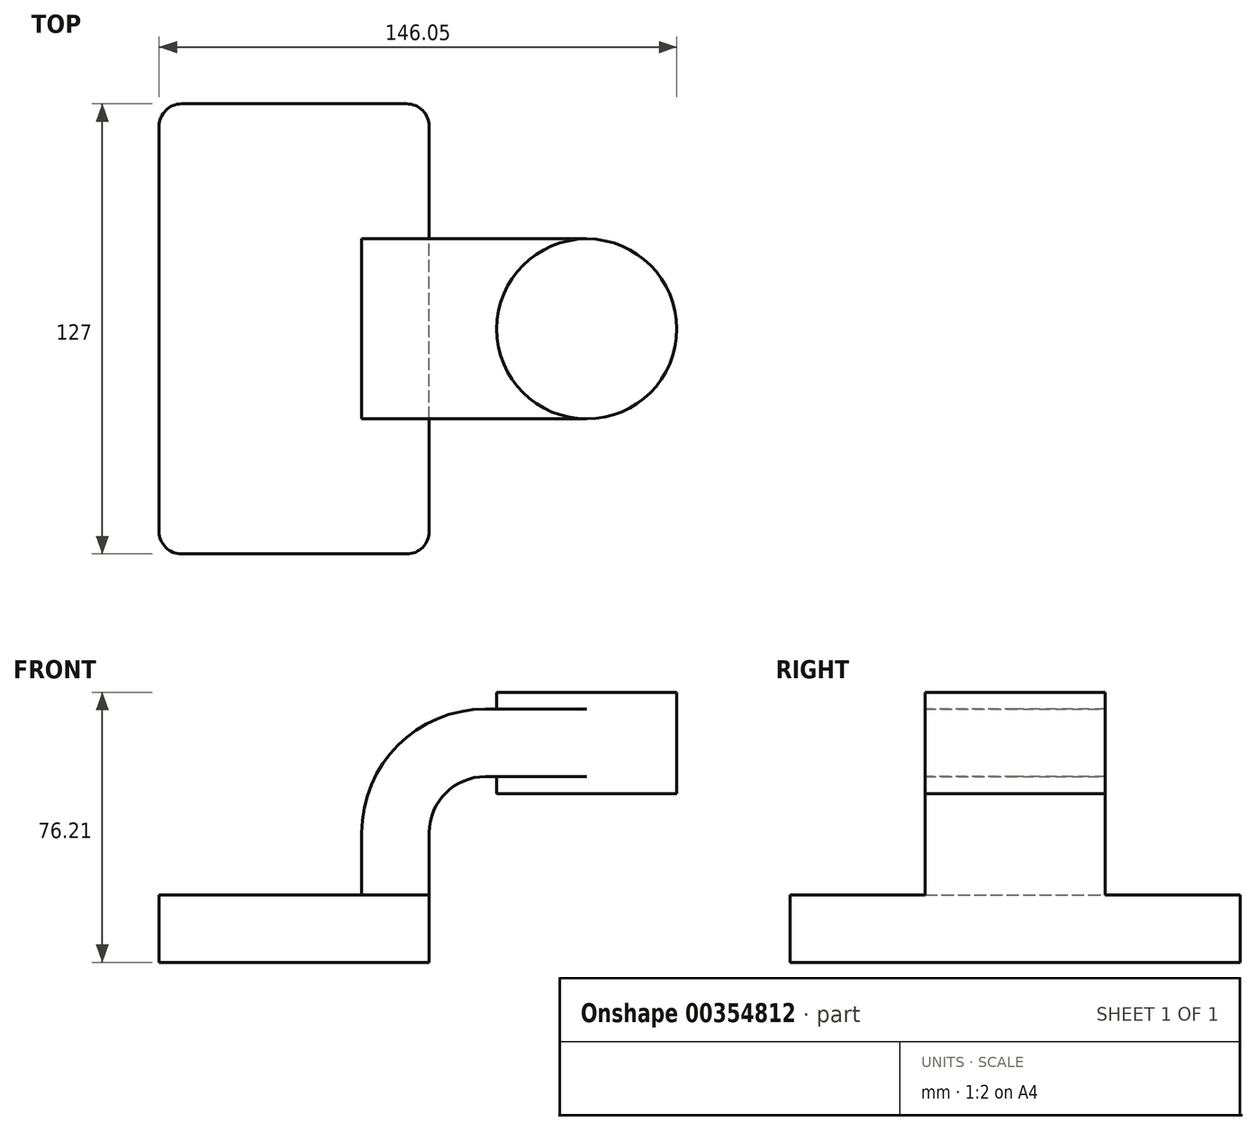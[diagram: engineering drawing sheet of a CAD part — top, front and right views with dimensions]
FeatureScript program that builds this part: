
annotation { "Feature Type Name" : "Feature", "Feature Type Description" : "" }
export const myFeature = defineFeature(function(context is Context, id is Id, definition is map)
    precondition{}
    {
        {
            var Q0;
            Q0=qCreatedBy(makeId("Front.planeOp"),FACE);
            var sketch = newSketch(context, id + "F0", { "sketchPlane" : qUnion([Q0])});
            skPoint(sketch, "E0.middle", {"position": v(0, 0) * mm});
            skLineSegment(sketch, "E1.bottom", {"start": v(-38.1, -9.53) * mm, "end": v(38.1, -9.53) * mm});
            skLineSegment(sketch, "E1.top", {"start": v(-38.1, 9.53) * mm, "end": v(38.1, 9.53) * mm});
            skLineSegment(sketch, "E1.left", {"start": v(-38.1, -9.53) * mm, "end": v(-38.1, 9.53) * mm});
            skLineSegment(sketch, "E1.right", {"start": v(38.1, -9.53) * mm, "end": v(38.1, 9.53) * mm});
            skLineSegment(sketch, "E2.bottom", {"start": v(57.15, 38.1) * mm, "end": v(107.95, 38.1) * mm});
            skLineSegment(sketch, "E2.top", {"start": v(57.15, 66.67) * mm, "end": v(107.95, 66.67) * mm});
            skLineSegment(sketch, "E2.left", {"start": v(57.15, 38.1) * mm, "end": v(57.15, 66.67) * mm});
            skLineSegment(sketch, "E2.right", {"start": v(107.95, 38.1) * mm, "end": v(107.95, 66.67) * mm});
            skPoint(sketch, "E2.middle", {"position": v(82.55, 52.39) * mm});
            skLineSegment(sketch, "E3", {"start": v(38.1, 9.53) * mm, "end": v(38.1, 27) * mm});
            skArc(sketch, "E4", {"start": v(38.1, 27) * mm, "mid": v(42.75, 38.23) * mm, "end": v(53.97, 42.88) * mm});
            skLineSegment(sketch, "E5", {"start": v(53.97, 42.88) * mm, "end": v(82.55, 42.88) * mm});
            skLineSegment(sketch, "E6.0", {"start": v(53.97, 61.93) * mm, "end": v(82.55, 61.93) * mm});
            skArc(sketch, "E6.1", {"start": v(19.05, 27) * mm, "mid": v(29.28, 51.7) * mm, "end": v(53.97, 61.93) * mm});
            skLineSegment(sketch, "E6.2", {"start": v(19.05, 9.53) * mm, "end": v(19.05, 27) * mm});
            skLineSegment(sketch, "E7", {"start": v(82.55, 38.1) * mm, "end": v(82.55, 66.67) * mm});
            skFitSpline(sketch, "E8", {"points": [v(-38.1, 9.53) * mm, v(53.97, 61.93) * mm], "startDerivative": vector(0, 103.77) * mm, "endDerivative": vector(112.87, 0) * mm});
            skSolve(sketch);
        }
        {
            var Q0;
            Q0=makeQuery(id+"F0.imprint","IMPRINT",FACE,{"disambiguationData":[TD([[makeQuery(id+"F0.imprint","IMPRINT",EDGE,{"derivedFrom":sQuery(id+"F0.wireOp",EDGE,"E1.bottom")}),1.0]])]});
            extrude(context, id + "F1", {"entities" : qUnion([Q0]), "endBound" : BoundingType.SYMMETRIC, "depth" : 127 * mm});
        }
        {
            var Q0;
            Q0=makeQuery(id+"F0.imprint","IMPRINT",FACE,{"disambiguationData":[TD([[makeQuery(id+"F0.imprint","IMPRINT",EDGE,{"derivedFrom":sQuery(id+"F0.wireOp",EDGE,"E6.1")}),1.0]])]});
            extrude(context, id + "F2", {"entities" : qUnion([Q0]), "operationType" : NewBodyOperationType.ADD, "endBound" : BoundingType.SYMMETRIC, "depth" : 15.88 * mm});
        }
        {
            var Q0;
            {var subQ1=sQuery(id+"F0.wireOp",EDGE,"E3");Q0=makeQuery(id+"F0.imprint","IMPRINT",FACE,{"disambiguationData":[TD([[makeQuery(id+"F0.imprint","IMPRINT",EDGE,{"derivedFrom":subQ1}),1.0]])]});}
            var Q1;
            {var subQ0=sQuery(id+"F0.wireOp",EDGE,"E5");var subQ1=sQuery(id+"F0.wireOp",EDGE,"E2.left");var subQ2=makeQuery(id+"F0.imprint","INTERSECT",VERTEX,{"derivedFrom":[subQ1,subQ0]});Q1=makeQuery(id+"F0.imprint","IMPRINT",FACE,{"disambiguationData":[TD([[makeQuery(id+"F0.imprint","IMPRINT",EDGE,{"disambiguationData":[TD([[subQ2,-1.0]])],"derivedFrom":subQ1}),-1.0]])]});}
            extrude(context, id + "F3", {"entities" : qUnion([Q0, Q1]), "operationType" : NewBodyOperationType.ADD, "endBound" : BoundingType.SYMMETRIC, "depth" : 50.8 * mm});
        }
        {
            var Q0;
            {var subQ0=sQuery(id+"F0.wireOp",EDGE,"E2.right");Q0=makeQuery(id+"F0.imprint","IMPRINT",FACE,{"disambiguationData":[TD([[makeQuery(id+"F0.imprint","IMPRINT",EDGE,{"derivedFrom":subQ0}),1.0]])]});}
            var Q1;
            Q1=sQuery(id+"F0.wireOp",EDGE,"E7");
            revolve(context, id + "F4", {"operationType" : NewBodyOperationType.ADD, "entities" : qUnion([Q0]), "axis" : qUnion([Q1]), "revolveType" : RevolveType.FULL});
        }
        {
            var Q0;
            Q0=makeQuery(id+"F1.opExtrude","CAP_EDGE",EDGE,{"disambiguationData":[OSD([sQuery(id+"F0.wireOp",EDGE,"E1.left")])],"isStart":false});
            var Q1;
            Q1=makeQuery(id+"F1.opExtrude","CAP_EDGE",EDGE,{"disambiguationData":[OSD([sQuery(id+"F0.wireOp",EDGE,"E1.right")])],"isStart":false});
            var Q2;
            Q2=makeQuery(id+"F1.opExtrude","CAP_EDGE",EDGE,{"disambiguationData":[OSD([sQuery(id+"F0.wireOp",EDGE,"E1.right")])],"isStart":true});
            var Q3;
            Q3=makeQuery(id+"F1.opExtrude","CAP_EDGE",EDGE,{"disambiguationData":[OSD([sQuery(id+"F0.wireOp",EDGE,"E1.left")])],"isStart":true});
            fillet(context, id + "F5", {"entities" : qUnion([Q0, Q1, Q2, Q3]), "radius" : 6.35 * mm, "tangentPropagation" : true, "allowEdgeOverflow" : false});
        }
    });
